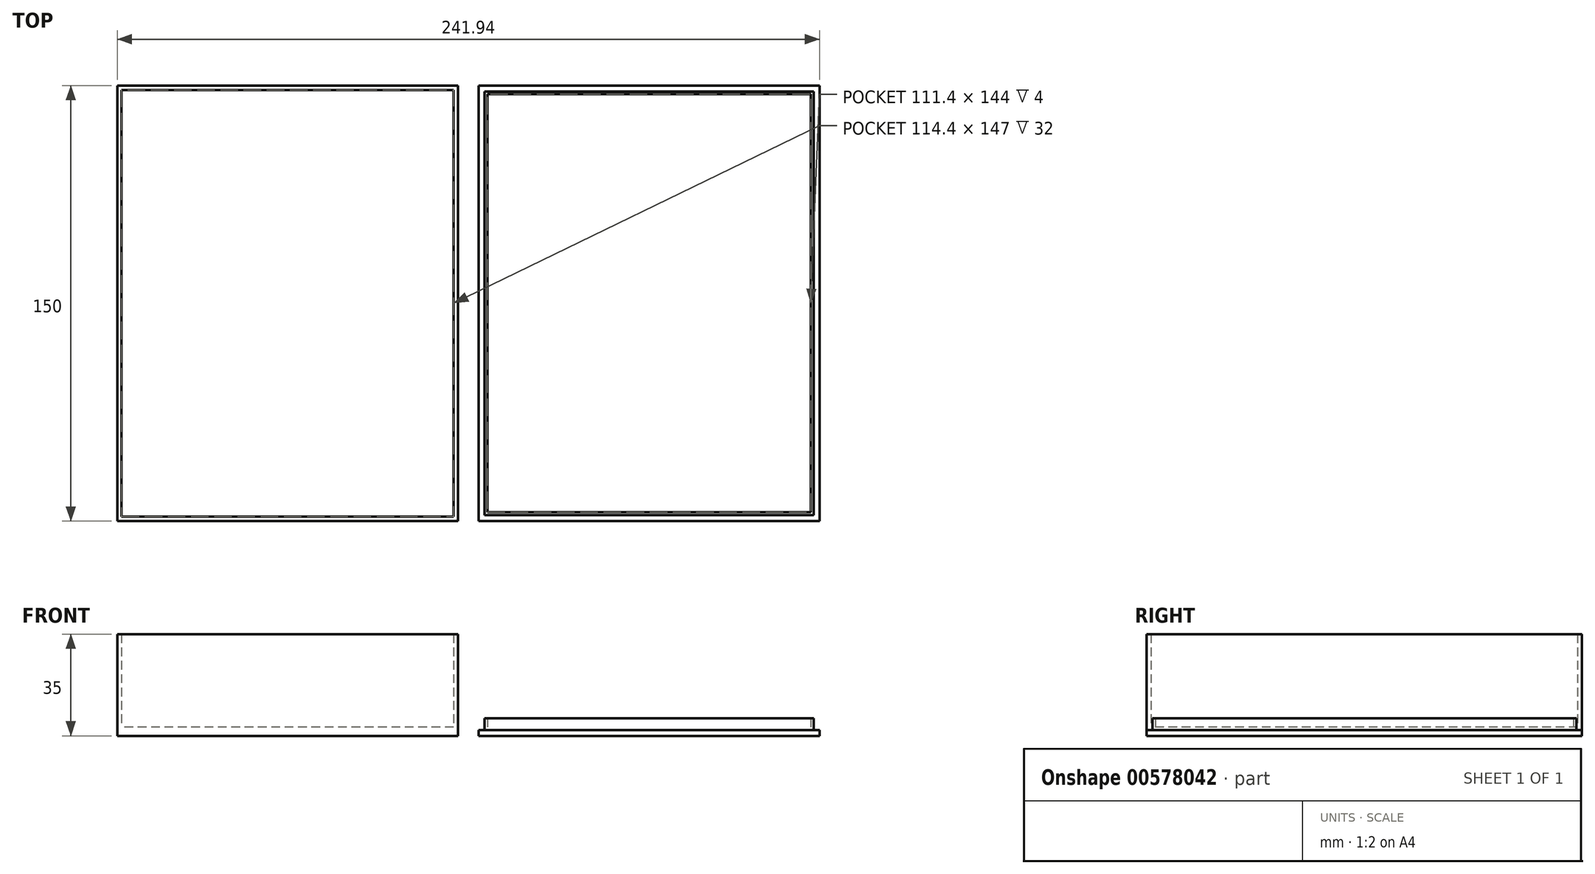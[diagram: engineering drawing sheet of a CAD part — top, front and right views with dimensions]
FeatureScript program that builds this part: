
annotation { "Feature Type Name" : "Feature", "Feature Type Description" : "" }
export const myFeature = defineFeature(function(context is Context, id is Id, definition is map)
    precondition{}
    {
        {
            var Q0;
            Q0=qCreatedBy(makeId("Top.planeOp"),FACE);
            var sketch = newSketch(context, id + "F0", { "sketchPlane" : qUnion([Q0])});
            skLineSegment(sketch, "E0.bottom", {"start": v(58.7, 75) * mm, "end": v(-58.7, 75) * mm});
            skLineSegment(sketch, "E0.top", {"start": v(58.7, -75) * mm, "end": v(-58.7, -75) * mm});
            skLineSegment(sketch, "E0.left", {"start": v(58.7, 75) * mm, "end": v(58.7, -75) * mm});
            skLineSegment(sketch, "E0.right", {"start": v(-58.7, 75) * mm, "end": v(-58.7, -75) * mm});
            skPoint(sketch, "E0.middle", {"position": v(0, 0) * mm});
            skLineSegment(sketch, "E1.bottom", {"start": v(57.2, 73.5) * mm, "end": v(-57.2, 73.5) * mm});
            skLineSegment(sketch, "E1.top", {"start": v(57.2, -73.5) * mm, "end": v(-57.2, -73.5) * mm});
            skLineSegment(sketch, "E1.left", {"start": v(57.2, 73.5) * mm, "end": v(57.2, -73.5) * mm});
            skLineSegment(sketch, "E1.right", {"start": v(-57.2, 73.5) * mm, "end": v(-57.2, -73.5) * mm});
            skSolve(sketch);
        }
        {
            var Q0;
            Q0=makeQuery(id+"F0.imprint","IMPRINT",FACE,{"disambiguationData":[TD([[makeQuery(id+"F0.imprint","IMPRINT",EDGE,{"derivedFrom":sQuery(id+"F0.wireOp",EDGE,"E0.bottom")}),1.0]])]});
            extrude(context, id + "F1", {"entities" : qUnion([Q0]), "depth" : 35 * mm, "offsetDistance" : 25 * mm});
        }
        {
            var Q0;
            Q0=qCreatedBy(makeId("Top.planeOp"),FACE);
            var sketch = newSketch(context, id + "F2", { "sketchPlane" : qUnion([Q0])});
            skLineSegment(sketch, "E2.bottom", {"start": v(58.7, 75) * mm, "end": v(-58.7, 75) * mm});
            skLineSegment(sketch, "E2.top", {"start": v(58.7, -75) * mm, "end": v(-58.7, -75) * mm});
            skLineSegment(sketch, "E2.left", {"start": v(58.7, 75) * mm, "end": v(58.7, -75) * mm});
            skLineSegment(sketch, "E2.right", {"start": v(-58.7, 75) * mm, "end": v(-58.7, -75) * mm});
            skPoint(sketch, "E2.middle", {"position": v(0, 0) * mm});
            skSolve(sketch);
        }
        {
            var Q0;
            Q0 = qSketchRegion(id + "F2", true);
            extrude(context, id + "F3", {"entities" : qUnion([Q0]), "operationType" : NewBodyOperationType.ADD, "depth" : 3 * mm, "offsetDistance" : 25 * mm});
        }
        {
            var Q0;
            Q0=qCreatedBy(makeId("Top.planeOp"),FACE);
            var sketch = newSketch(context, id + "F4", { "sketchPlane" : qUnion([Q0])});
            skLineSegment(sketch, "E3.bottom", {"start": v(183.24, 75) * mm, "end": v(65.84, 75) * mm});
            skLineSegment(sketch, "E3.top", {"start": v(183.24, -75) * mm, "end": v(65.84, -75) * mm});
            skLineSegment(sketch, "E3.left", {"start": v(183.24, 75) * mm, "end": v(183.24, -75) * mm});
            skLineSegment(sketch, "E3.right", {"start": v(65.84, 75) * mm, "end": v(65.84, -75) * mm});
            skPoint(sketch, "E3.middle", {"position": v(124.54, 0) * mm});
            skLineSegment(sketch, "E4.bottom", {"start": v(181.24, 73) * mm, "end": v(67.84, 73) * mm});
            skLineSegment(sketch, "E4.top", {"start": v(181.24, -73) * mm, "end": v(67.84, -73) * mm});
            skLineSegment(sketch, "E4.left", {"start": v(181.24, 73) * mm, "end": v(181.24, -73) * mm});
            skLineSegment(sketch, "E4.right", {"start": v(67.84, 73) * mm, "end": v(67.84, -73) * mm});
            skLineSegment(sketch, "E5.bottom", {"start": v(180.24, 72) * mm, "end": v(68.84, 72) * mm});
            skLineSegment(sketch, "E5.top", {"start": v(180.24, -72) * mm, "end": v(68.84, -72) * mm});
            skLineSegment(sketch, "E5.left", {"start": v(180.24, 72) * mm, "end": v(180.24, -72) * mm});
            skLineSegment(sketch, "E5.right", {"start": v(68.84, 72) * mm, "end": v(68.84, -72) * mm});
            skSolve(sketch);
        }
        {
            var Q0;
            Q0=makeQuery(id+"F4.imprint","IMPRINT",FACE,{"disambiguationData":[TD([[makeQuery(id+"F4.imprint","IMPRINT",EDGE,{"derivedFrom":sQuery(id+"F4.wireOp",EDGE,"E4.bottom")}),1.0]])]});
            extrude(context, id + "F5", {"entities" : qUnion([Q0]), "depth" : 6 * mm, "offsetDistance" : 25 * mm});
        }
        {
            var Q0;
            Q0=makeQuery(id+"F4.imprint","IMPRINT",FACE,{"disambiguationData":[TD([[makeQuery(id+"F4.imprint","IMPRINT",EDGE,{"derivedFrom":sQuery(id+"F4.wireOp",EDGE,"E3.bottom")}),1.0]])]});
            var Q1;
            Q1=makeQuery(id+"F4.imprint","IMPRINT",FACE,{"disambiguationData":[TD([[makeQuery(id+"F4.imprint","IMPRINT",EDGE,{"derivedFrom":sQuery(id+"F4.wireOp",EDGE,"E5.bottom")}),1.0]])]});
            extrude(context, id + "F6", {"entities" : qUnion([Q0, Q1]), "operationType" : NewBodyOperationType.ADD, "depth" : 2 * mm, "offsetDistance" : 25 * mm});
        }
    });
